# Revit family: xxxPost_Hydrant-Pedal_Operated-Murdock_Mfg-M-2000
name_source: partatom
category: Plumbing Fixtures
units: mm (PartAtom-declared; Revit-internal decimal feet)

## family parameters
Cut with Voids When Loaded = No
Host = Face
OmniClass Number = 23.45.05.14.99
OmniClass Title = Other Sanitary Washing Plumbing Fixtures
Part Type = Normal
Room Calculation Point = No
Round Connector Dimension = Use Diameter
Shared = No

## types (1)
- M-2000
    -BFH Double Ball Check Valve and Vacuum Breaker = No
    -R01 Shut Off Valve with Plate = No
    -VB Vacuum Breaker = No
    2 ft. (61 cm) Depth of Bury = No
    3 ft. (91.4 cm) Depth of Bury = No
    4 ft. (121.9 cm) Depth of Bury = No
    5 ft. (152.4 cm) Depth of Bury = No
    6 ft. (182.9 cm) Depth of Bury = No
    Activation = Pedal-Operated
    Assembly Code = D2020300
    Bury Depth = 12"
    CW Connection = Yes
    CWFU = 0
    Default Elevation = 0"
    Depth of Bury = 0"
    Description = 3/4" Freeze Resistant, Self-Closing Pedal Operated Post Hydrant
    Finish = Iron Casting-Murdock-Green Enamel
    Finish- Nozzle = Brass-Murdock-Yellow
    HW Connection = No
    HWFU = 0
    Height = 30"
    IAPMO Compliance = Member of U.S. Green Building Council, Recyclable Product, o ASTM
standards B61 and B62
    Installation Instruction Link = https://www.murdockmfg.com
    Installation Type = Floor Mounted
    Manufacturer = Murdock Manufacturing
    Material = Iron Casting-Murdock-Green Enamel
    Model = M-2000
    NPT Connection Diameter = 3/4"
    Other (Depth of Bury) = 0"
    Plain End Spout = No
    Product Documentation Link = https://www.murdockmfg.com
    Product Page URL = https://www.murdockmfg.com
    Sewer Drain Connection = No
    URL = https://www.murdockmfg.com
    Vent Connection = No
    WFU = 0
    Waste Connection = No

## geometry (parser evidence)
native form markers: Sweep x2
no freeform markers — native parametric forms only
